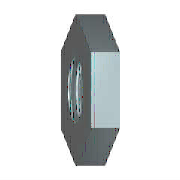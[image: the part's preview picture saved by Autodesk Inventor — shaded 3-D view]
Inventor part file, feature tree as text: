
AUTODESK INVENTOR PART (.ipt)
format: ipt  version: 2022 (Build 260153000, 153)  size: 126,976 bytes
history: native  units: mm (DEFAULTED — no unit token found)
features: hole x1, other x1, plane x1, sketch x1
ambient origin geometry x7: Origin, YZ Plane, XZ Plane, X Axis, Y Axis, Z Axis, Center Point
bodies: Solid1 (feature_tree), Body (feature_tree)
feature tree (4):
  hole  "Thread"  [1 undecoded]
  other  "Work Axis1"
  plane  "Work Plane1"
  sketch  "Sketch1"  dims[d0=6.350853mm d1=1.78mm d2=0.0mm d3=2.459mm d4=6.0mm d5=4.0mm d6=2.0mm d7=14.3117mm d8=8.0mm d9=20.594885mm d10=0.270633mm d11=30.0deg d12=0.270633mm d13=30.0deg d15=0.0mm d17=0.0mm d18=0.270633mm d19=0.270633mm d20=0.0mm d21=0.0mm]
note: 1 required parameter value undecoded (feature->parameter linkage not recoverable at this tier; creation-order binding heuristic only, values carry confidence <= 0.55)
